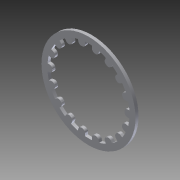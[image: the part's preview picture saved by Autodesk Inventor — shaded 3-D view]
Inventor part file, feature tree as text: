
AUTODESK INVENTOR PART (.ipt)
format: ipt  version: 2011 SP1 (Build 150282100, 282)  size: 188,928 bytes
history: native  units: in
note: dims shown in document units (in); Inventor stores cm internally (conversion verified against a paired STEP export)
features: other x7, extrude x1, sketch x1
ambient origin geometry x8: Origin, YZ Plane, XZ Plane, XY Plane, X Axis, Y Axis, Z Axis, Center Point
bodies: Solid1 (feature_tree)
feature tree (9):
  extrude  "Extrusion1"  [1 undecoded]
  other  "lockwasher_XY"
  other  "lockwasher_YZ"
  other  "lockwasher_ZX"
  other  "lockwasher_X"
  other  "lockwasher_Y"
  other  "lockwasher_Z"
  other  "lockwasher_Center"
  sketch  "Sketch_2"  dims[d0=0.02in d1=0.0in]
note: 1 required parameter value undecoded (feature->parameter linkage not recoverable at this tier; creation-order binding heuristic only, values carry confidence <= 0.55)
